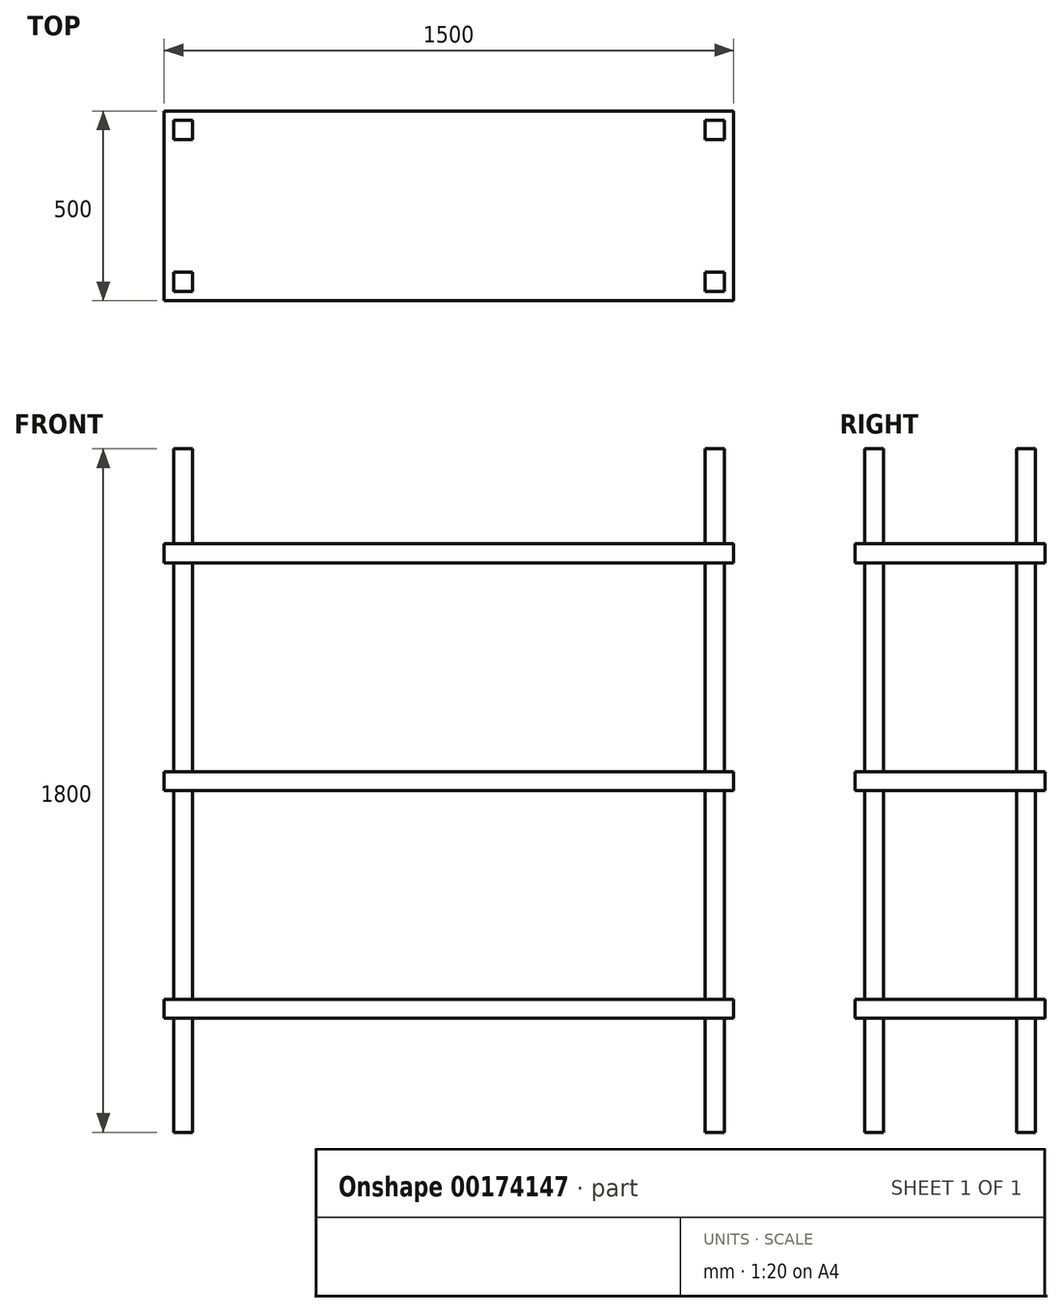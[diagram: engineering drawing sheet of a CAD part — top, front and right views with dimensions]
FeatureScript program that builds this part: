
annotation { "Feature Type Name" : "Feature", "Feature Type Description" : "" }
export const myFeature = defineFeature(function(context is Context, id is Id, definition is map)
    precondition{}
    {
        {
            var Q0;
            Q0=qCreatedBy(makeId("Top.planeOp"),FACE);
            cPlane(context, id + "F0", {"entities" : qUnion([Q0]), "cplaneType" : CPlaneType.OFFSET, "offset" : 300 * mm, "width" : 150 * mm, "height" : 150 * mm});
        }
        {
            var Q0;
            Q0=qCreatedBy(id+"F0.planeOp",FACE);
            var sketch = newSketch(context, id + "F1", { "sketchPlane" : qUnion([Q0])});
            skLineSegment(sketch, "E0.bottom", {"start": v(0, 0) * mm, "end": v(1500, 0) * mm});
            skLineSegment(sketch, "E0.top", {"start": v(0, 500) * mm, "end": v(1500, 500) * mm});
            skLineSegment(sketch, "E0.left", {"start": v(0, 0) * mm, "end": v(0, 500) * mm});
            skLineSegment(sketch, "E0.right", {"start": v(1500, 0) * mm, "end": v(1500, 500) * mm});
            skSolve(sketch);
        }
        {
            var Q0;
            Q0=makeQuery(id+"F1.imprint","IMPRINT",FACE,{"disambiguationData":[TD([[makeQuery(id+"F1.imprint","IMPRINT",EDGE,{"derivedFrom":sQuery(id+"F1.wireOp",EDGE,"E0.bottom")}),1.0]])]});
            extrude(context, id + "F2", {"entities" : qUnion([Q0]), "depth" : 50 * mm});
        }
        {
            var Q0;
            Q0=qCreatedBy(makeId("Top.planeOp"),FACE);
            var sketch = newSketch(context, id + "F3", { "sketchPlane" : qUnion([Q0])});
            skLineSegment(sketch, "E1.bottom", {"start": v(25, 75) * mm, "end": v(75, 75) * mm});
            skLineSegment(sketch, "E1.top", {"start": v(25, 25) * mm, "end": v(75, 25) * mm});
            skLineSegment(sketch, "E1.left", {"start": v(25, 75) * mm, "end": v(25, 25) * mm});
            skLineSegment(sketch, "E1.right", {"start": v(75, 75) * mm, "end": v(75, 25) * mm});
            skLineSegment(sketch, "E2.0.1.0", {"start": v(75, 475) * mm, "end": v(75, 425) * mm});
            skLineSegment(sketch, "E2.0.1.1", {"start": v(25, 475) * mm, "end": v(25, 425) * mm});
            skLineSegment(sketch, "E2.0.1.2", {"start": v(25, 475) * mm, "end": v(75, 475) * mm});
            skLineSegment(sketch, "E2.0.1.3", {"start": v(25, 425) * mm, "end": v(75, 425) * mm});
            skLineSegment(sketch, "E2.1.0.0", {"start": v(1475, 75) * mm, "end": v(1475, 25) * mm});
            skLineSegment(sketch, "E2.1.0.1", {"start": v(1425, 75) * mm, "end": v(1425, 25) * mm});
            skLineSegment(sketch, "E2.1.0.2", {"start": v(1425, 75) * mm, "end": v(1475, 75) * mm});
            skLineSegment(sketch, "E2.1.0.3", {"start": v(1425, 25) * mm, "end": v(1475, 25) * mm});
            skLineSegment(sketch, "E2.1.1.0", {"start": v(1475, 475) * mm, "end": v(1475, 425) * mm});
            skLineSegment(sketch, "E2.1.1.1", {"start": v(1425, 475) * mm, "end": v(1425, 425) * mm});
            skLineSegment(sketch, "E2.1.1.2", {"start": v(1425, 475) * mm, "end": v(1475, 475) * mm});
            skLineSegment(sketch, "E2.1.1.3", {"start": v(1425, 425) * mm, "end": v(1475, 425) * mm});
            skLineSegment(sketch, "E2.direction1", {"start": v(25, 25) * mm, "end": v(1425, 25) * mm, "construction": true});
            skLineSegment(sketch, "E2.direction2", {"start": v(25, 25) * mm, "end": v(25, 425) * mm, "construction": true});
            skSolve(sketch);
        }
        {
            var Q0;
            Q0=makeQuery(id+"F3.imprint","IMPRINT",FACE,{"disambiguationData":[TD([[makeQuery(id+"F3.imprint","IMPRINT",EDGE,{"derivedFrom":sQuery(id+"F3.wireOp",EDGE,"E1.bottom")}),-1.0]])]});
            var Q1;
            Q1=makeQuery(id+"F3.imprint","IMPRINT",FACE,{"disambiguationData":[TD([[makeQuery(id+"F3.imprint","IMPRINT",EDGE,{"derivedFrom":sQuery(id+"F3.wireOp",EDGE,"E2.1.0.0")}),-1.0]])]});
            var Q2;
            Q2=makeQuery(id+"F3.imprint","IMPRINT",FACE,{"disambiguationData":[TD([[makeQuery(id+"F3.imprint","IMPRINT",EDGE,{"derivedFrom":sQuery(id+"F3.wireOp",EDGE,"E2.1.1.0")}),-1.0]])]});
            var Q3;
            Q3=makeQuery(id+"F3.imprint","IMPRINT",FACE,{"disambiguationData":[TD([[makeQuery(id+"F3.imprint","IMPRINT",EDGE,{"derivedFrom":sQuery(id+"F3.wireOp",EDGE,"E2.0.1.0")}),-1.0]])]});
            extrude(context, id + "F4", {"entities" : qUnion([Q0, Q1, Q2, Q3]), "operationType" : NewBodyOperationType.ADD, "depth" : 1800 * mm});
        }
        {
            var Q0;
            Q0=qCreatedBy(id+"F0.planeOp",FACE);
            cPlane(context, id + "F5", {"entities" : qUnion([Q0]), "cplaneType" : CPlaneType.OFFSET, "offset" : 600 * mm, "width" : 150 * mm, "height" : 150 * mm});
        }
        {
            var Q0;
            Q0=qCreatedBy(id+"F5.planeOp",FACE);
            var sketch = newSketch(context, id + "F6", { "sketchPlane" : qUnion([Q0])});
            skLineSegment(sketch, "E3.0.0", {"start": v(0, 500) * mm, "end": v(0, 0) * mm});
            skLineSegment(sketch, "E3.0.1", {"start": v(0, 0) * mm, "end": v(1500, 0) * mm});
            skLineSegment(sketch, "E3.0.2", {"start": v(1500, 0) * mm, "end": v(1500, 500) * mm});
            skLineSegment(sketch, "E3.0.3", {"start": v(1500, 500) * mm, "end": v(0, 500) * mm});
            skLineSegment(sketch, "E3.1", {"start": v(0, 0) * mm, "end": v(1500, 0) * mm});
            skSolve(sketch);
        }
        {
            var Q0;
            Q0=makeQuery(id+"F6.imprint","IMPRINT",FACE,{"disambiguationData":[TD([[makeQuery(id+"F6.imprint","IMPRINT",EDGE,{"derivedFrom":sQuery(id+"F6.wireOp",EDGE,"E3.0.0")}),1.0]])]});
            extrude(context, id + "F7", {"entities" : qUnion([Q0]), "operationType" : NewBodyOperationType.ADD, "depth" : 50 * mm});
        }
        {
            var Q0;
            Q0=qCreatedBy(id+"F5.planeOp",FACE);
            cPlane(context, id + "F8", {"entities" : qUnion([Q0]), "cplaneType" : CPlaneType.OFFSET, "offset" : 600 * mm, "width" : 150 * mm, "height" : 150 * mm});
        }
        {
            var Q0;
            Q0=qCreatedBy(id+"F8.planeOp",FACE);
            var sketch = newSketch(context, id + "F9", { "sketchPlane" : qUnion([Q0])});
            skLineSegment(sketch, "E4.0", {"start": v(0, 0) * mm, "end": v(1500, 0) * mm});
            skLineSegment(sketch, "E5.0.0", {"start": v(1500, 500) * mm, "end": v(0, 500) * mm});
            skLineSegment(sketch, "E5.0.1", {"start": v(0, 500) * mm, "end": v(0, 0) * mm});
            skLineSegment(sketch, "E5.0.3", {"start": v(1500, 0) * mm, "end": v(1500, 500) * mm});
            skSolve(sketch);
        }
        {
            var Q0;
            Q0=makeQuery(id+"F9.imprint","IMPRINT",FACE,{"disambiguationData":[TD([[makeQuery(id+"F9.imprint","IMPRINT",EDGE,{"derivedFrom":sQuery(id+"F9.wireOp",EDGE,"E5.0.0")}),1.0]])]});
            extrude(context, id + "F10", {"entities" : qUnion([Q0]), "operationType" : NewBodyOperationType.ADD, "depth" : 50 * mm});
        }
    });
